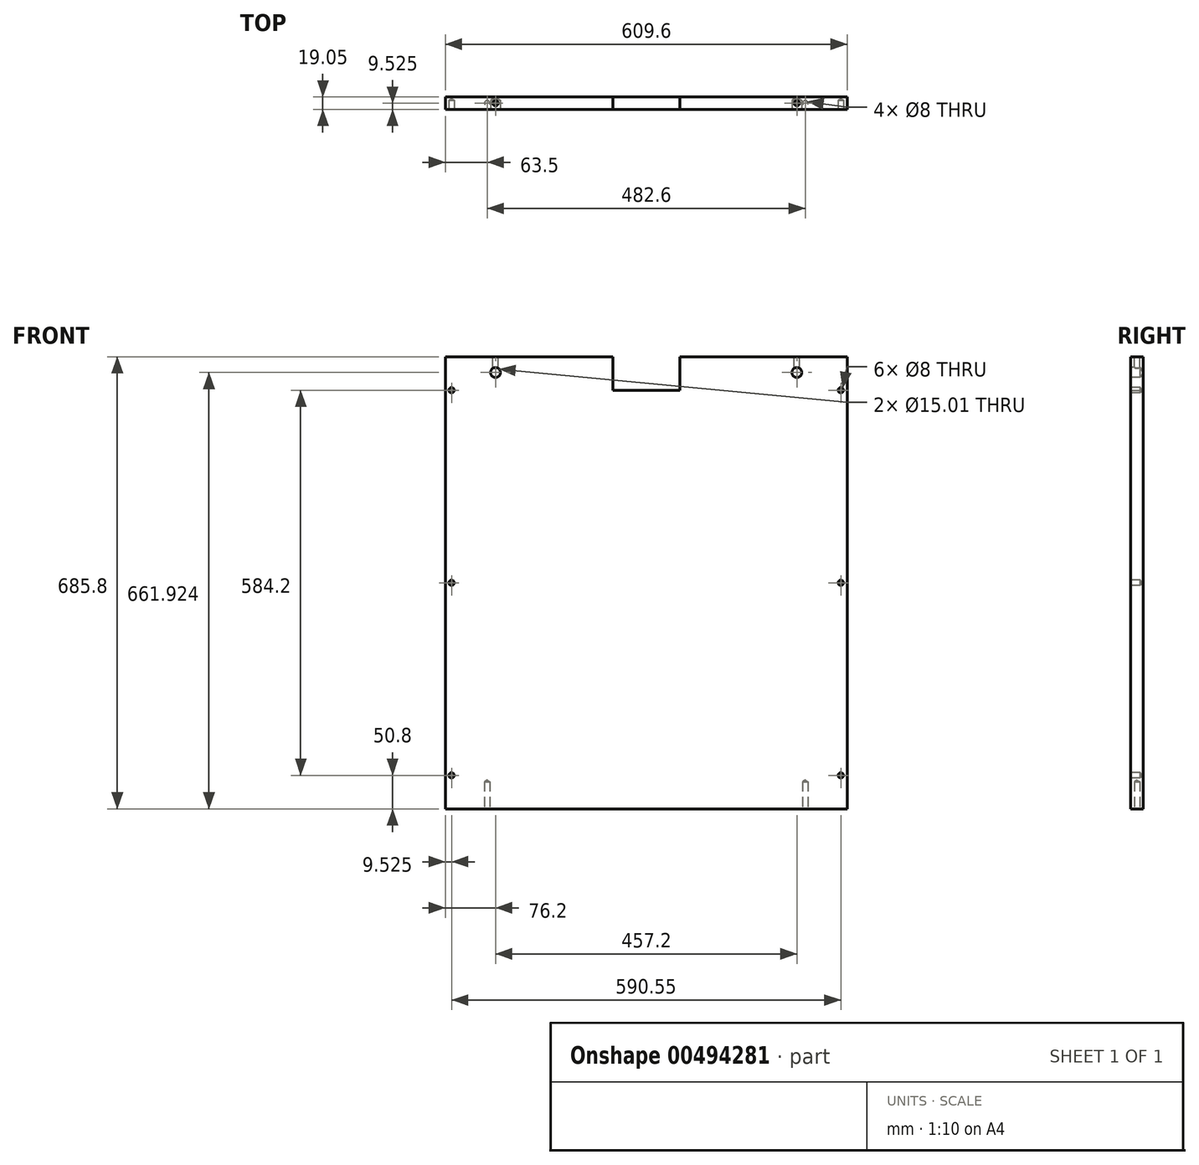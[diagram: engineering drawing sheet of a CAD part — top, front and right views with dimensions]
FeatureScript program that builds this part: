
annotation { "Feature Type Name" : "Feature", "Feature Type Description" : "" }
export const myFeature = defineFeature(function(context is Context, id is Id, definition is map)
    precondition{}
    {
        {
            var Q0;
            Q0=qCreatedBy(makeId("Front.planeOp"),FACE);
            var sketch = newSketch(context, id + "F0", { "sketchPlane" : qUnion([Q0])});
            skLineSegment(sketch, "E0.top", {"start": v(304.8, -342.9) * mm, "end": v(-304.8, -342.9) * mm});
            skLineSegment(sketch, "E0.left", {"start": v(304.8, 342.9) * mm, "end": v(304.8, -342.9) * mm});
            skLineSegment(sketch, "E0.right", {"start": v(-304.8, 342.9) * mm, "end": v(-304.8, -342.9) * mm});
            skPoint(sketch, "E0.middle", {"position": v(0, 0) * mm});
            skLineSegment(sketch, "E1.bottom", {"start": v(50.8, 292.1) * mm, "end": v(-50.8, 292.1) * mm});
            skLineSegment(sketch, "E2", {"start": v(-50.8, 342.9) * mm, "end": v(-50.8, 292.1) * mm});
            skLineSegment(sketch, "E3", {"start": v(50.8, 342.9) * mm, "end": v(50.8, 292.1) * mm});
            skLineSegment(sketch, "E4", {"start": v(-50.8, 342.9) * mm, "end": v(-304.8, 342.9) * mm});
            skLineSegment(sketch, "E5", {"start": v(50.8, 342.9) * mm, "end": v(304.8, 342.9) * mm});
            skSolve(sketch);
        }
        {
            var Q0;
            Q0=makeQuery(id+"F0.imprint","IMPRINT",FACE,{"disambiguationData":[TD([[makeQuery(id+"F0.imprint","IMPRINT",EDGE,{"derivedFrom":sQuery(id+"F0.wireOp",EDGE,"E0.top")}),-1.0]])]});
            extrude(context, id + "F1", {"entities" : qUnion([Q0]), "depth" : 19.05 * mm});
        }
        {
            var Q0;
            Q0=makeQuery(id+"F1.opExtrude","CAP_FACE",FACE,{"disambiguationData":[OSD([sQuery(id+"F0.wireOp",EDGE,"E0.top"),sQuery(id+"F0.wireOp",EDGE,"E0.left"),sQuery(id+"F0.wireOp",EDGE,"E0.right"),sQuery(id+"F0.wireOp",EDGE,"E1.bottom"),sQuery(id+"F0.wireOp",EDGE,"E2"),sQuery(id+"F0.wireOp",EDGE,"E3"),sQuery(id+"F0.wireOp",EDGE,"E4"),sQuery(id+"F0.wireOp",EDGE,"E5")])],"isStart":false});
            var sketch = newSketch(context, id + "F2", { "sketchPlane" : qUnion([Q0])});
            skPoint(sketch, "E6", {"position": v(-228.6, 319.02) * mm});
            skPoint(sketch, "E7", {"position": v(228.6, 319.02) * mm});
            skSolve(sketch);
        }
        {
            var Q0;
            Q0=sQuery(id+"F2.wireOp",VERTEX,"E6");
            var Q1;
            Q1=sQuery(id+"F2.wireOp",VERTEX,"E7");
            var Q2;
            Q2=makeQuery(id+"F1.opExtrude","SWEPT_BODY",BODY,{"disambiguationData":[OSD([sQuery(id+"F0.wireOp",EDGE,"E0.top"),sQuery(id+"F0.wireOp",EDGE,"E0.left"),sQuery(id+"F0.wireOp",EDGE,"E0.right"),sQuery(id+"F0.wireOp",EDGE,"E1.bottom"),sQuery(id+"F0.wireOp",EDGE,"E2"),sQuery(id+"F0.wireOp",EDGE,"E3"),sQuery(id+"F0.wireOp",EDGE,"E4"),sQuery(id+"F0.wireOp",EDGE,"E5")])]});
            hole(context, id + "F3", {"style" : HoleStyle.SIMPLE, "endStyle" : HoleEndStyle.BLIND, "holeDiameter" : 15 * mm, "holeDepth" : 14.22 * mm, "isTappedThrough" : true, "tappedDepth" : 12.7 * mm, "tapClearance" : 3, "startFromSketch" : true, "locations" : qUnion([Q0, Q1]), "scope" : qUnion([Q2])});
        }
        {
            var Q0;
            Q0=makeQuery(id+"F1.opExtrude","SWEPT_FACE",FACE,{"disambiguationData":[OSD([sQuery(id+"F0.wireOp",EDGE,"E4")])]});
            var sketch = newSketch(context, id + "F4", { "sketchPlane" : qUnion([Q0])});
            skPoint(sketch, "E8", {"position": v(-228.6, -9.53) * mm});
            skSolve(sketch);
        }
        {
            var Q0;
            Q0=makeQuery(id+"F1.opExtrude","SWEPT_FACE",FACE,{"disambiguationData":[OSD([sQuery(id+"F0.wireOp",EDGE,"E5")])]});
            var sketch = newSketch(context, id + "F5", { "sketchPlane" : qUnion([Q0])});
            skPoint(sketch, "E9", {"position": v(228.6, -9.53) * mm});
            skSolve(sketch);
        }
        {
            var Q0;
            Q0=sQuery(id+"F4.wireOp",VERTEX,"E8");
            var Q1;
            Q1=sQuery(id+"F5.wireOp",VERTEX,"E9");
            var Q2;
            Q2=makeQuery(id+"F1.opExtrude","SWEPT_BODY",BODY,{"disambiguationData":[OSD([sQuery(id+"F0.wireOp",EDGE,"E0.top"),sQuery(id+"F0.wireOp",EDGE,"E0.left"),sQuery(id+"F0.wireOp",EDGE,"E0.right"),sQuery(id+"F0.wireOp",EDGE,"E1.bottom"),sQuery(id+"F0.wireOp",EDGE,"E2"),sQuery(id+"F0.wireOp",EDGE,"E3"),sQuery(id+"F0.wireOp",EDGE,"E4"),sQuery(id+"F0.wireOp",EDGE,"E5")])]});
            hole(context, id + "F6", {"style" : HoleStyle.SIMPLE, "endStyle" : HoleEndStyle.BLIND, "holeDiameter" : 8 * mm, "holeDepth" : 25.4 * mm, "isTappedThrough" : true, "tappedDepth" : 12.7 * mm, "tapClearance" : 3, "startFromSketch" : true, "locations" : qUnion([Q0, Q1]), "scope" : qUnion([Q2])});
        }
        {
            var Q0;
            Q0=makeQuery(id+"F1.opExtrude","CAP_FACE",FACE,{"disambiguationData":[OSD([sQuery(id+"F0.wireOp",EDGE,"E0.top"),sQuery(id+"F0.wireOp",EDGE,"E0.left"),sQuery(id+"F0.wireOp",EDGE,"E0.right"),sQuery(id+"F0.wireOp",EDGE,"E1.bottom"),sQuery(id+"F0.wireOp",EDGE,"E2"),sQuery(id+"F0.wireOp",EDGE,"E3"),sQuery(id+"F0.wireOp",EDGE,"E4"),sQuery(id+"F0.wireOp",EDGE,"E5")])],"isStart":false});
            var sketch = newSketch(context, id + "F7", { "sketchPlane" : qUnion([Q0])});
            skLineSegment(sketch, "E10", {"start": v(-304.8, 342.9) * mm, "end": v(-295.28, 342.9) * mm});
            skPoint(sketch, "E11", {"position": v(-295.28, 292.1) * mm});
            skPoint(sketch, "E12", {"position": v(-295.27, -292.1) * mm});
            skPoint(sketch, "E13", {"position": v(-295.27, 0) * mm});
            skLineSegment(sketch, "E14", {"start": v(304.8, 342.9) * mm, "end": v(295.27, 342.9) * mm});
            skPoint(sketch, "E15", {"position": v(295.27, 292.1) * mm});
            skPoint(sketch, "E16", {"position": v(295.27, -292.1) * mm});
            skPoint(sketch, "E17", {"position": v(295.27, 0) * mm});
            skSolve(sketch);
        }
        {
            var Q0;
            Q0=sQuery(id+"F7.wireOp",VERTEX,"E11");
            var Q1;
            Q1=sQuery(id+"F7.wireOp",VERTEX,"E13");
            var Q2;
            Q2=sQuery(id+"F7.wireOp",VERTEX,"E12");
            var Q3;
            Q3=sQuery(id+"F7.wireOp",VERTEX,"E16");
            var Q4;
            Q4=sQuery(id+"F7.wireOp",VERTEX,"E17");
            var Q5;
            Q5=sQuery(id+"F7.wireOp",VERTEX,"E15");
            var Q6;
            Q6=makeQuery(id+"F1.opExtrude","SWEPT_BODY",BODY,{"disambiguationData":[OSD([sQuery(id+"F0.wireOp",EDGE,"E0.top"),sQuery(id+"F0.wireOp",EDGE,"E0.left"),sQuery(id+"F0.wireOp",EDGE,"E0.right"),sQuery(id+"F0.wireOp",EDGE,"E1.bottom"),sQuery(id+"F0.wireOp",EDGE,"E2"),sQuery(id+"F0.wireOp",EDGE,"E3"),sQuery(id+"F0.wireOp",EDGE,"E4"),sQuery(id+"F0.wireOp",EDGE,"E5")])]});
            hole(context, id + "F8", {"style" : HoleStyle.SIMPLE, "endStyle" : HoleEndStyle.BLIND, "holeDiameter" : 8 * mm, "holeDepth" : 14.22 * mm, "isTappedThrough" : true, "tappedDepth" : 12.7 * mm, "tapClearance" : 3, "startFromSketch" : true, "locations" : qUnion([Q0, Q1, Q2, Q3, Q4, Q5]), "scope" : qUnion([Q6])});
        }
        {
            var Q0;
            Q0=makeQuery(id+"F1.opExtrude","SWEPT_FACE",FACE,{"disambiguationData":[OSD([sQuery(id+"F0.wireOp",EDGE,"E0.top")])]});
            var sketch = newSketch(context, id + "F9", { "sketchPlane" : qUnion([Q0])});
            skPoint(sketch, "E18", {"position": v(-241.3, 9.53) * mm});
            skPoint(sketch, "E19", {"position": v(241.3, 9.53) * mm});
            skSolve(sketch);
        }
        {
            var Q0;
            Q0=sQuery(id+"F9.wireOp",VERTEX,"E18");
            var Q1;
            Q1=sQuery(id+"F9.wireOp",VERTEX,"E19");
            var Q2;
            Q2=makeQuery(id+"F1.opExtrude","SWEPT_BODY",BODY,{"disambiguationData":[OSD([sQuery(id+"F0.wireOp",EDGE,"E0.top"),sQuery(id+"F0.wireOp",EDGE,"E0.left"),sQuery(id+"F0.wireOp",EDGE,"E0.right"),sQuery(id+"F0.wireOp",EDGE,"E1.bottom"),sQuery(id+"F0.wireOp",EDGE,"E2"),sQuery(id+"F0.wireOp",EDGE,"E3"),sQuery(id+"F0.wireOp",EDGE,"E4"),sQuery(id+"F0.wireOp",EDGE,"E5")])]});
            hole(context, id + "F10", {"style" : HoleStyle.SIMPLE, "endStyle" : HoleEndStyle.BLIND, "holeDiameter" : 8 * mm, "holeDepth" : 41.27 * mm, "isTappedThrough" : true, "tappedDepth" : 12.7 * mm, "tapClearance" : 3, "startFromSketch" : true, "locations" : qUnion([Q0, Q1]), "scope" : qUnion([Q2])});
        }
    });
